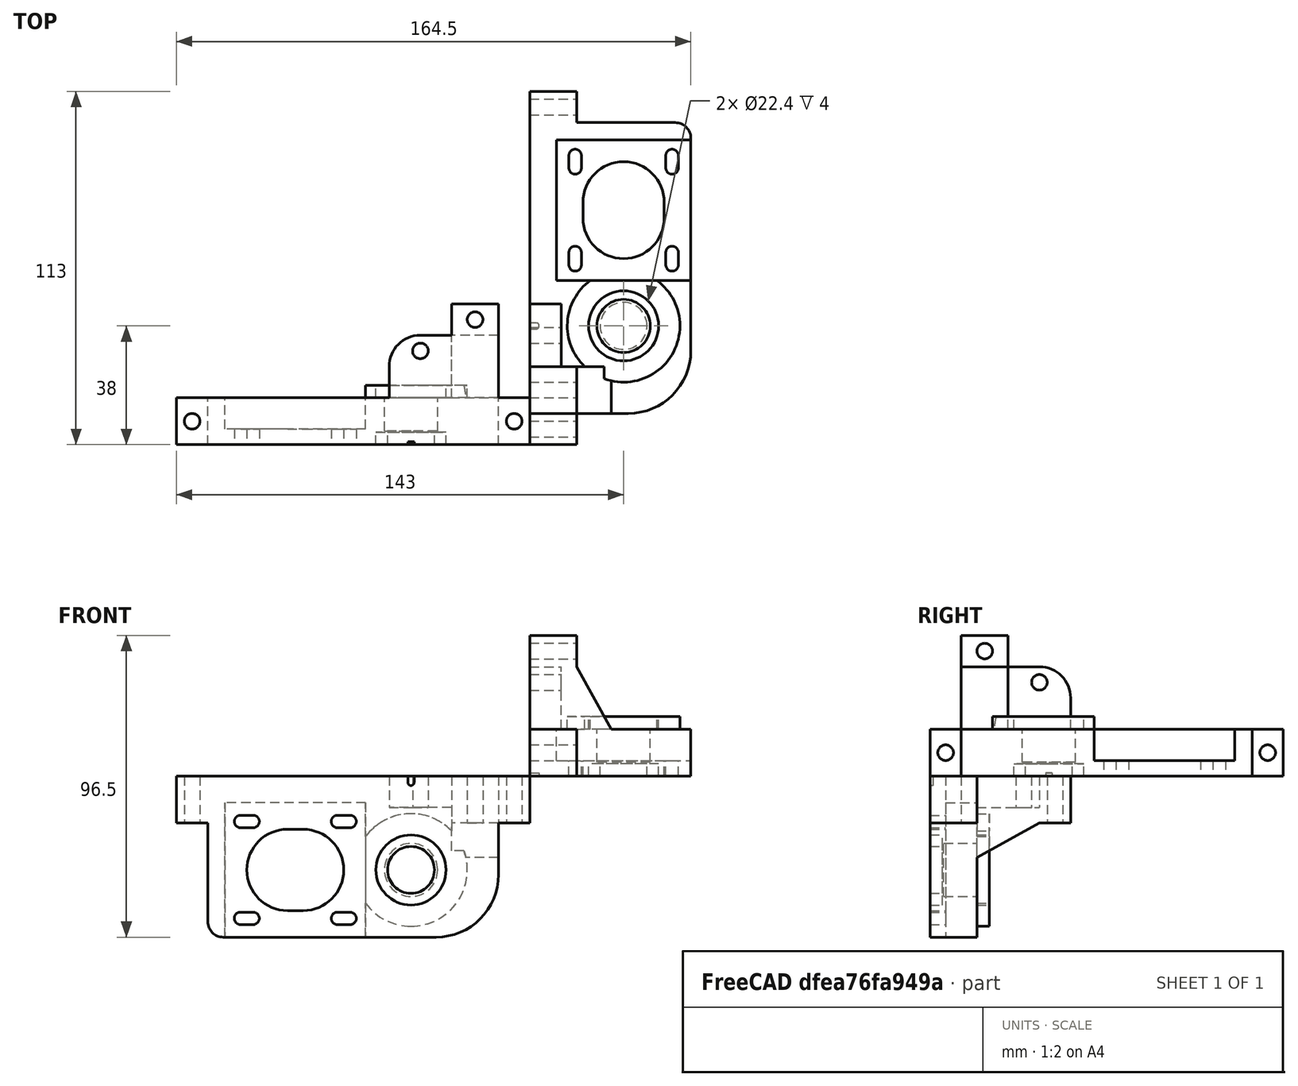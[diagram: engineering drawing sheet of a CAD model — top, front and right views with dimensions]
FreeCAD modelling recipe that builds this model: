
FCSTD DOCUMENT  (FreeCAD 0.15R4527 (Git))
Label: y_motor_holder
License: All rights reserved
LicenseURL: http://en.wikipedia.org/wiki/All_rights_reserved
objects: Part::Cylinder×9, Part::Cut×9, Part::MultiFuse×8, Part::Box×6, Part::Extrusion×6, Sketcher::SketchObject×4, Part::Fillet×3, Part::Feature×2, Mesh::Feature×1, Part::Chamfer×1
note: 48 computed .brp shape members not serialized (recipe doc carries the construction recipe); baked Part::Feature solids carry a one-line shape summary decoded from their .brp

FEATURE [Mesh::Feature] Ymotorholder
FEATURE [Part::Feature] Ymotorholder001001  label="Ymotorholder002"
  shape: bbox 51.5 x 113 x 45 mm, 1264 faces, 0 solids (baked)
FEATURE [Part::Box] Box  label="Cubo"
  Height = 15
  Length = 15
  Width = 113
FEATURE [Part::Box] Box001  label="Cubo001"
  Height = 15
  Length = 36.5
  Placement = pos=(15,10,0) rot=(0,0,1;0rad)
  Width = 93
FEATURE [Part::Fillet] Fillet
  Base = -> Box001
  Edges = 1 edges r=20: [Edge5]
FEATURE [Part::Fillet] Fillet001
  Base = -> Fillet
  Edges = 1 edges r=5: [Edge3]
FEATURE [Part::Cylinder] Cylinder  label="Cilindro"
  Angle = 360
  Height = 15
  Placement = pos=(30,38,4.4) rot=(0,0,1;0rad)
  Radius = 8.5
FEATURE [Part::Cut] Cut
  Base = -> Fillet001
  Tool = -> Cylinder
FEATURE [Part::Cylinder] Cylinder001  label="Cilindro001"
  Angle = 360
  Height = 4
  Placement = pos=(30,38,0) rot=(0,0,1;0rad)
  Radius = 7.5
FEATURE [Part::Cylinder] Cylinder002  label="Cilindro002"
  Angle = 360
  Height = 4
  Placement = pos=(30,38,0) rot=(0,0,1;0rad)
  Radius = 11.2
FEATURE [Part::Cut] Cut001
  Base = -> Cut
  Tool = -> Cylinder002
FEATURE [Part::MultiFuse] Fusion
  Shapes = -> [Cut001,Cylinder001]
FEATURE [Part::Cylinder] Cylinder003  label="Cilindro003"
  Angle = 360
  Height = 4
  Placement = pos=(30,38,15) rot=(0,0,1;0rad)
  Radius = 18
FEATURE [Part::Cylinder] Cylinder004  label="Cilindro004"
  Angle = 360
  Height = 4
  Placement = pos=(30,38,15) rot=(0,0,1;0rad)
  Radius = 11.2
FEATURE [Part::Cut] Cut002
  Base = -> Cylinder003
  Tool = -> Cylinder004
FEATURE [Part::MultiFuse] Fusion001
  Shapes = -> [Cut002,Fusion]
FEATURE [Part::Cylinder] Cylinder005  label="Cilindro005"
  Angle = 360
  Height = 17
  Placement = pos=(-1,5,7.5) rot=(0,1,0;1.5708rad)
  Radius = 2.5
FEATURE [Part::Cylinder] Cylinder006  label="Cilindro006"
  Angle = 360
  Height = 17
  Placement = pos=(-1,108,7.5) rot=(0,1,0;1.5708rad)
  Radius = 2.5
FEATURE [Part::MultiFuse] Fusion002
  Shapes = -> [Cylinder005,Cylinder006]
FEATURE [Part::Cut] Cut003
  Base = -> Box
  Tool = -> Fusion002
FEATURE [Part::MultiFuse] Fusion003
  Shapes = -> [Fusion001,Cut003]
FEATURE [Part::Box] Box002  label="Cubo002"
  Height = 30
  Length = 15
  Placement = pos=(0,10,15) rot=(0,0,1;0rad)
  Width = 15
FEATURE [Part::Box] Box003  label="Cubo003"
  Height = 20
  Length = 11
  Placement = pos=(15,10,15) rot=(0,0,1;0rad)
  Width = 15
FEATURE [Part::Box] Box004  label="Cubo004"
  Height = 20
  Length = 10
  Placement = pos=(0,25,15) rot=(0,0,1;0rad)
  Width = 20
FEATURE [Part::Fillet] Fillet002
  Base = -> Box004
  Edges = 1 edges r=10: [Edge12]
FEATURE [Part::Chamfer] Chamfer
  Base = -> Box003
  Edges = 1 edges: [Edge6 r1=19.99 r2=10.99]
FEATURE [Part::Cylinder] Cylinder007  label="Cilindro007"
  Angle = 360
  Height = 17
  Placement = pos=(-1,17.5,40) rot=(0,1,0;1.5708rad)
  Radius = 2.5
FEATURE [Part::Cylinder] Cylinder008  label="Cilindro008"
  Angle = 360
  Height = 17
  Placement = pos=(-1,35,30) rot=(0,1,0;1.5708rad)
  Radius = 2.5
FEATURE [Part::MultiFuse] Fusion004
  Shapes = -> [Cylinder007,Cylinder008]
FEATURE [Part::MultiFuse] Fusion005
  Shapes = -> [Box002,Chamfer,Fillet002]
FEATURE [Part::Cut] Cut004
  Base = -> Fusion005
  Tool = -> Fusion004
FEATURE [Part::MultiFuse] Fusion006
  Shapes = -> [Fusion003,Cut004]
FEATURE [Part::Box] Box005  label="Cubo005"
  Height = 14
  Length = 43
  Placement = pos=(8.5,52.5,5) rot=(0,0,1;0rad)
  Width = 45
FEATURE [Part::Cut] Cut005
  Base = -> Fusion006
  Tool = -> Box005
FEATURE [Sketcher::SketchObject] Sketch
  ExternalGeometry = -> [Ymotorholder001001]
  Placement = pos=(0,0,0) rot=(1,0,0;3.14159rad)
  Support = -> Ymotorholder001001 [Face234]
  sketch-geometry (4):
    g0: ArcOfCircle CenterX=14.5 CenterY=-57.5 CenterZ=0 NormalX=0 NormalY=0 NormalZ=1 Radius=2 StartAngle=0 EndAngle=3.14159
    g1: ArcOfCircle CenterX=14.5 CenterY=-61.5 CenterZ=0 NormalX=0 NormalY=0 NormalZ=1 Radius=2 StartAngle=3.14159 EndAngle=6.28319
    g2: LineSegment StartX=12.5 StartY=-57.5 StartZ=0 EndX=12.5 EndY=-61.5 EndZ=0
    g3: LineSegment StartX=16.5 StartY=-57.5 StartZ=0 EndX=16.5 EndY=-61.5 EndZ=0
  constraints (8):
    c: Tangent(g0,g3) = 1.5708
    c: Tangent(g0,g2) = -1.5708
    c: Tangent(g2,g1) = -1.5708
    c: Tangent(g3,g1) = 1.5708
    c: Equal(g0,g1)
    c: Coincident(g0,g-4)
    c: Coincident(g0,g-3)
    c: Coincident(g1,g-7)
FEATURE [Part::Extrusion] Extrude
  Base = -> Sketch
  Dir = (0,0,10)
  Placement = pos=(0,0,-1) rot=(0,0,1;0rad)
  Solid = true
FEATURE [Sketcher::SketchObject] Sketch001
  Placement = pos=(0,0,0) rot=(1,0,0;3.14159rad)
  sketch-geometry (4):
    g0: ArcOfCircle CenterX=14.5 CenterY=-57.5 CenterZ=0 NormalX=0 NormalY=0 NormalZ=1 Radius=2 StartAngle=0 EndAngle=3.14159
    g1: ArcOfCircle CenterX=14.5 CenterY=-61.5 CenterZ=0 NormalX=0 NormalY=0 NormalZ=1 Radius=2 StartAngle=3.14159 EndAngle=6.28319
    g2: LineSegment StartX=12.5 StartY=-57.5 StartZ=0 EndX=12.5 EndY=-61.5 EndZ=0
    g3: LineSegment StartX=16.5 StartY=-57.5 StartZ=0 EndX=16.5 EndY=-61.5 EndZ=0
  constraints (5):
    c: Tangent(g0,g3) = 1.5708
    c: Tangent(g0,g2) = -1.5708
    c: Tangent(g2,g1) = -1.5708
    c: Tangent(g3,g1) = 1.5708
    c: Equal(g0,g1)
FEATURE [Part::Extrusion] Extrude001
  Base = -> Sketch001
  Dir = (0,0,10)
  Placement = pos=(0,31,-1) rot=(0,0,1;0rad)
  Solid = true
FEATURE [Part::Extrusion] Extrude002
  Base = -> Sketch001
  Dir = (0,0,10)
  Placement = pos=(31,31,-1) rot=(0,0,1;0rad)
  Solid = true
FEATURE [Part::Extrusion] Extrude003
  Base = -> Sketch001
  Dir = (0,0,10)
  Placement = pos=(31,0,-1) rot=(0,0,1;0rad)
  Solid = true
FEATURE [Part::MultiFuse] Fusion007
  Shapes = -> [Extrude,Extrude001,Extrude002,Extrude003]
FEATURE [Part::Cut] Cut006
  Base = -> Cut005
  Tool = -> Fusion007
FEATURE [Sketcher::SketchObject] Sketch002
  ExternalGeometry = -> [Ymotorholder001001]
  Placement = pos=(0,0,0) rot=(1,0,0;3.14159rad)
  Support = -> Ymotorholder001001 [Face234]
  sketch-geometry (4):
    g0: ArcOfCircle CenterX=30 CenterY=-72.5 CenterZ=0 NormalX=0 NormalY=0 NormalZ=1 Radius=13 StartAngle=0 EndAngle=3.14159
    g1: ArcOfCircle CenterX=30 CenterY=-77.5 CenterZ=0 NormalX=0 NormalY=0 NormalZ=1 Radius=13 StartAngle=3.14159 EndAngle=6.28319
    g2: LineSegment StartX=17 StartY=-72.5 StartZ=0 EndX=17 EndY=-77.5 EndZ=0
    g3: LineSegment StartX=43 StartY=-72.5 StartZ=0 EndX=43 EndY=-77.5 EndZ=0
  constraints (8):
    c: Tangent(g0,g3) = 1.5708
    c: Tangent(g0,g2) = -1.5708
    c: Tangent(g2,g1) = -1.5708
    c: Tangent(g3,g1) = 1.5708
    c: Equal(g0,g1)
    c: Coincident(g-3,g0)
    c: Coincident(g0,g-4)
    c: Coincident(g1,g-3)
FEATURE [Part::Extrusion] Extrude004
  Base = -> Sketch002
  Dir = (0,0,10)
  Placement = pos=(0,0,-1) rot=(0,0,1;0rad)
  Solid = true
FEATURE [Part::Cut] Cut007
  Base = -> Cut006
  Tool = -> Extrude004
FEATURE [Sketcher::SketchObject] Sketch003
  ExternalGeometry = -> [Ymotorholder001001]
  Placement = pos=(0,0,0) rot=(1,0,0;3.14159rad)
  Support = -> Ymotorholder001001 [Face234]
  sketch-geometry (6):
    g0: LineSegment StartX=1.90735e-06 StartY=-37 StartZ=0 EndX=2 EndY=-37 EndZ=0
    g1: LineSegment StartX=1.90735e-06 StartY=-39 StartZ=0 EndX=2 EndY=-39 EndZ=0
    g2: ArcOfCircle CenterX=2 CenterY=-38 CenterZ=0 NormalX=0 NormalY=0 NormalZ=1 Radius=1 StartAngle=4.71239 EndAngle=7.85398
    g3: LineSegment StartX=1.90735e-06 StartY=-37 StartZ=0 EndX=-0.499998 EndY=-37 EndZ=0
    g4: LineSegment StartX=1.90735e-06 StartY=-39 StartZ=0 EndX=-0.499998 EndY=-39 EndZ=0
    g5: LineSegment StartX=-0.499998 StartY=-39 StartZ=0 EndX=-0.499998 EndY=-37 EndZ=0
  constraints (16):
    c: Coincident(g0,g-3)
    c: Coincident(g0,g-6)
    c: Coincident(g1,g-4)
    c: Horizontal(g1)
    c: Coincident(g2,g0)
    c: Coincident(g2,g1)
    c: PointOnObject(g-5,g2)
    c: Radius(g2) = 1
    c: Coincident(g3,g0)
    c: Horizontal(g3)
    c: Coincident(g4,g1)
    c: Horizontal(g4)
    c: Coincident(g5,g4)
    c: Coincident(g5,g3)
    c: Vertical(g5)
    c: DistanceX(g3) = -0.5
FEATURE [Part::Extrusion] Extrude005
  Base = -> Sketch003
  Dir = (0,0,1)
  Solid = true
FEATURE [Part::Cut] Cut008  label="y_motor_holder"
  Base = -> Cut007
  Tool = -> Extrude005
FEATURE [Part::Feature] Cut009  label="y_motor_holder001"
  Placement = pos=(0,0,0) rot=(-0.57735,0.57735,0.57735;2.0944rad)
  shape: bbox 113 x 45 x 51.5 mm, 67 faces (baked)
